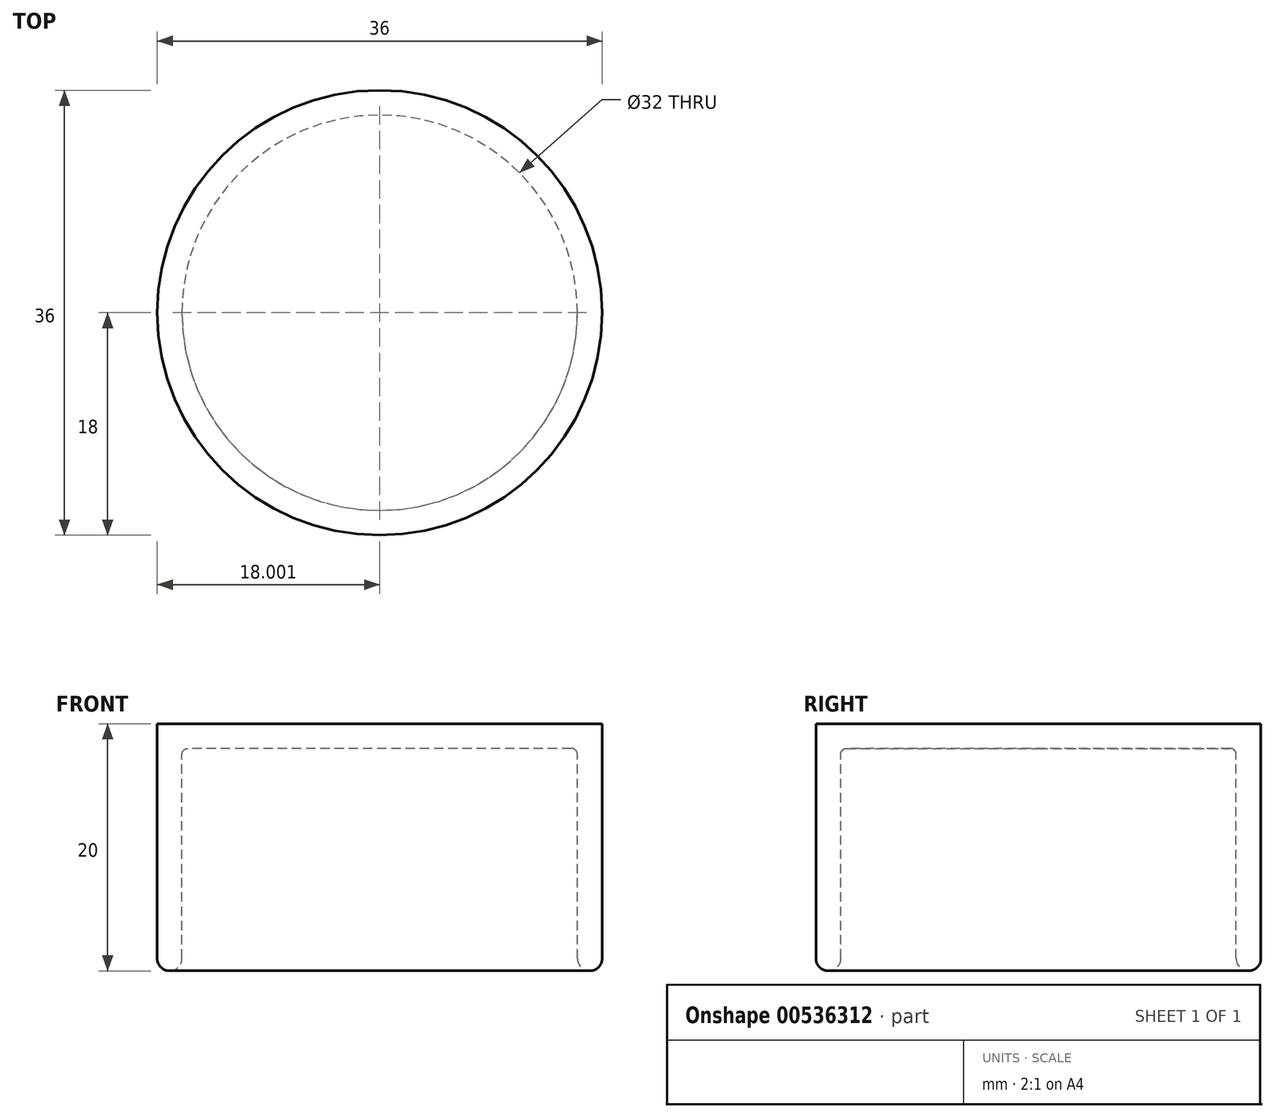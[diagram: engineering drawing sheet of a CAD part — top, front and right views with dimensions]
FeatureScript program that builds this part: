
annotation { "Feature Type Name" : "Feature", "Feature Type Description" : "" }
export const myFeature = defineFeature(function(context is Context, id is Id, definition is map)
    precondition{}
    {
        {
            var Q0;
            Q0=qCreatedBy(makeId("Front.planeOp"),FACE);
            var sketch = newSketch(context, id + "F0", { "sketchPlane" : qUnion([Q0])});
            skLineSegment(sketch, "E0.top", {"start": v(-8.9, -21.44) * mm, "end": v(-6.9, -21.44) * mm});
            skLineSegment(sketch, "E0.left", {"start": v(-8.9, -1.44) * mm, "end": v(-8.9, -21.44) * mm});
            skLineSegment(sketch, "E1", {"start": v(9.1, -1.44) * mm, "end": v(-8.9, -1.44) * mm});
            skLineSegment(sketch, "E2", {"start": v(9.1, -1.44) * mm, "end": v(9.1, -3.44) * mm});
            skLineSegment(sketch, "E3", {"start": v(9.1, -3.44) * mm, "end": v(-6.9, -3.44) * mm});
            skLineSegment(sketch, "E4", {"start": v(-6.9, -3.44) * mm, "end": v(-6.9, -21.44) * mm});
            skSolve(sketch);
        }
        {
            var Q0;
            Q0=qSketchRegion(id+"F0",true);
            var Q1;
            Q1=sQuery(id+"F0.wireOp",EDGE,"E2");
            revolve(context, id + "F1", {"entities" : qUnion([Q0]), "axis" : qUnion([Q1]), "revolveType" : RevolveType.FULL});
        }
        {
            var Q0;
            Q0=makeQuery(id+"F1.opRevolve","SWEPT_FACE",FACE,{"disambiguationData":[OSD([sQuery(id+"F0.wireOp",EDGE,"E3")])]});
            fillet(context, id + "F2", {"entities" : qUnion([Q0]), "radius" : 0.5 * mm, "tangentPropagation" : true, "allowEdgeOverflow" : false});
        }
        {
            var Q0;
            Q0=makeQuery(id+"F1.opRevolve","SWEPT_FACE",FACE,{"disambiguationData":[OSD([sQuery(id+"F0.wireOp",EDGE,"E0.top")])]});
            fillet(context, id + "F3", {"entities" : qUnion([Q0]), "radius" : 1 * mm, "tangentPropagation" : true, "allowEdgeOverflow" : false});
        }
    });
